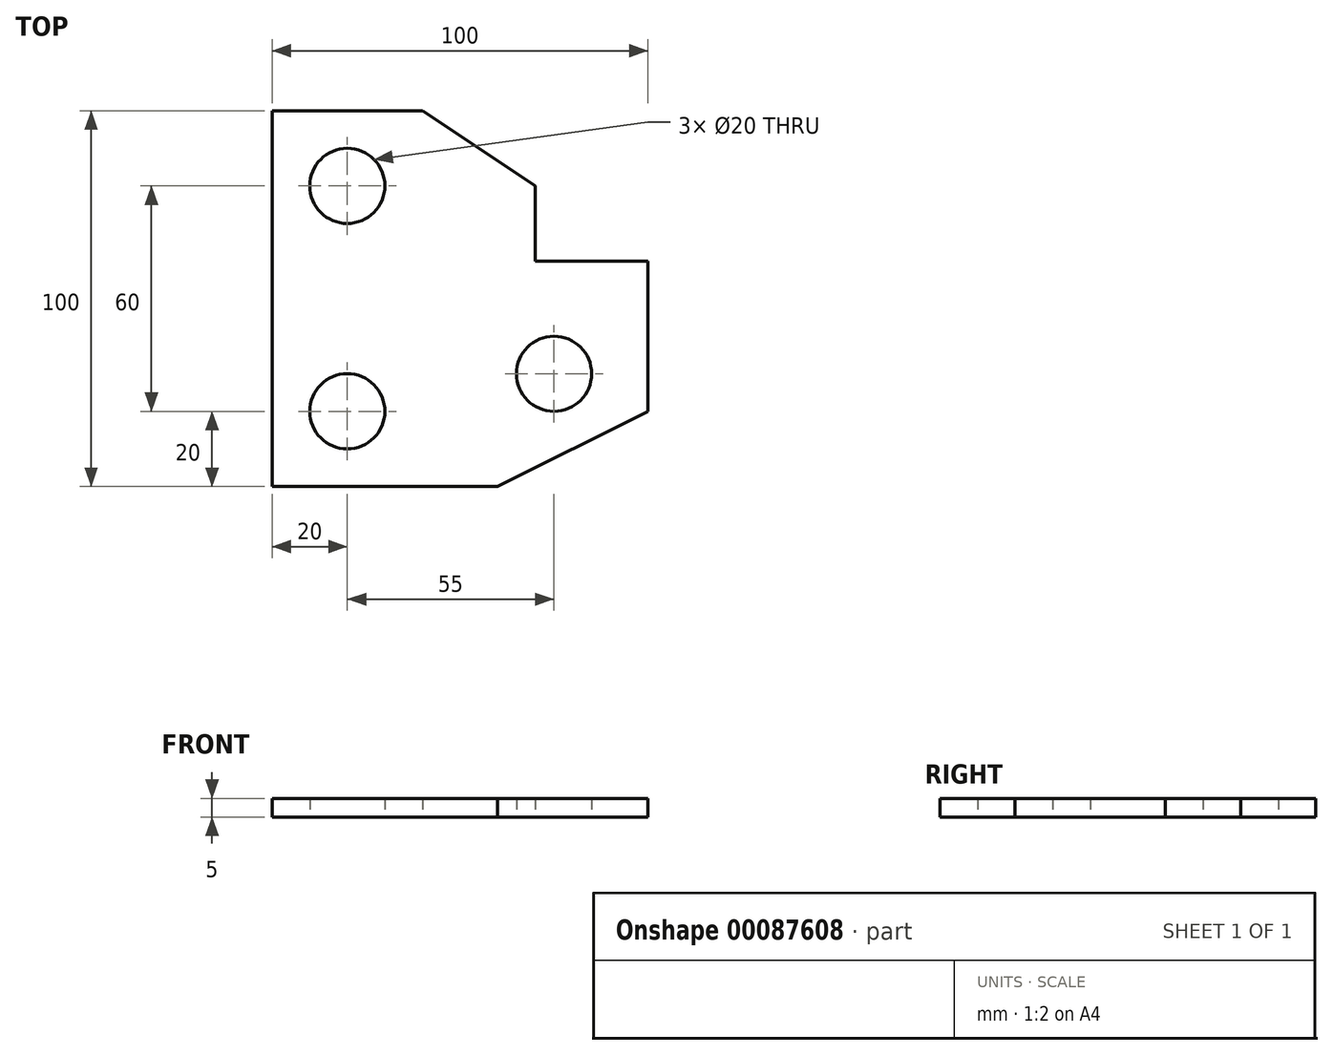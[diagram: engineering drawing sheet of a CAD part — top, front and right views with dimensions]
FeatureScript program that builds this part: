
annotation { "Feature Type Name" : "Feature", "Feature Type Description" : "" }
export const myFeature = defineFeature(function(context is Context, id is Id, definition is map)
    precondition{}
    {
        {
            var Q0;
            Q0=qCreatedBy(makeId("Top.planeOp"),FACE);
            var sketch = newSketch(context, id + "F0", { "sketchPlane" : qUnion([Q0])});
            skLineSegment(sketch, "E0.bottom", {"start": v(0, 0) * mm, "end": v(60, 0) * mm});
            skLineSegment(sketch, "E0.top", {"start": v(0, 100) * mm, "end": v(40, 100) * mm});
            skLineSegment(sketch, "E0.left", {"start": v(0, 0) * mm, "end": v(0, 100) * mm});
            skLineSegment(sketch, "E0.right", {"start": v(100, 20) * mm, "end": v(100, 60) * mm});
            skLineSegment(sketch, "E1", {"start": v(60, 0) * mm, "end": v(100, 20) * mm});
            skLineSegment(sketch, "E2", {"start": v(100, 60) * mm, "end": v(70, 60) * mm});
            skLineSegment(sketch, "E3", {"start": v(70, 60) * mm, "end": v(70, 80) * mm});
            skLineSegment(sketch, "E4", {"start": v(70, 80) * mm, "end": v(40, 100) * mm});
            skCircle(sketch, "E5", {"center": v(20, 80) * mm, "radius": 10 * mm});
            skCircle(sketch, "E6", {"center": v(20, 20) * mm, "radius": 10 * mm});
            skCircle(sketch, "E7", {"center": v(75, 30) * mm, "radius": 10 * mm});
            skLineSegment(sketch, "E8", {"start": v(20, 20) * mm, "end": v(20, 80) * mm, "construction": true});
            skSolve(sketch);
        }
        {
            var Q0;
            Q0 = qSketchRegion(id + "F0", true);
            extrude(context, id + "F1", {"entities" : qUnion([Q0]), "depth" : 5 * mm});
        }
    });
